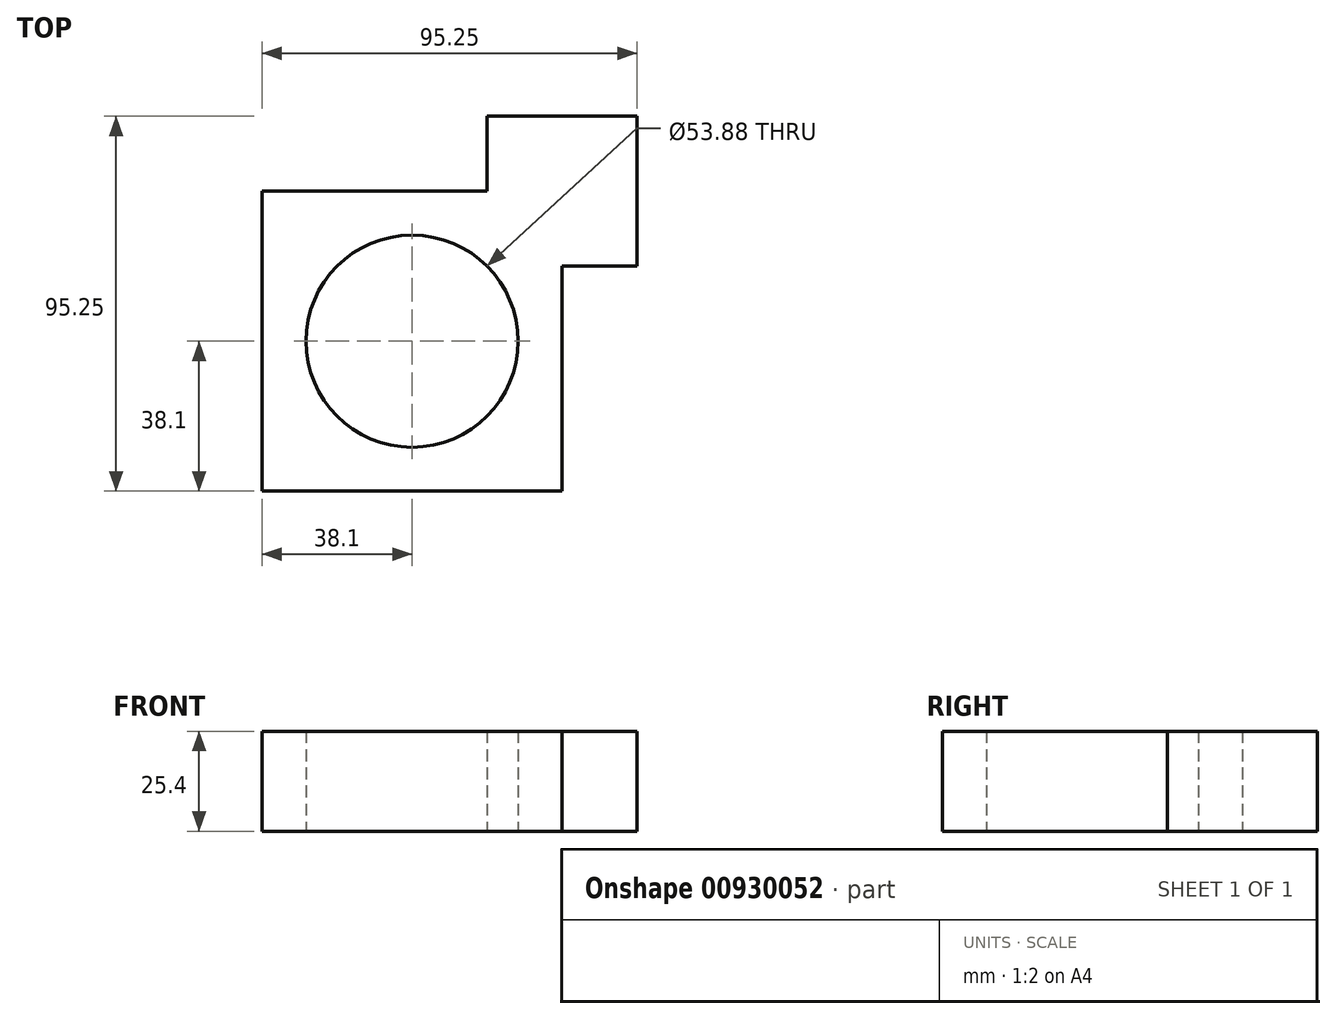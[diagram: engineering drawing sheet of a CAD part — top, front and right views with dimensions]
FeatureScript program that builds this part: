
annotation { "Feature Type Name" : "Feature", "Feature Type Description" : "" }
export const myFeature = defineFeature(function(context is Context, id is Id, definition is map)
    precondition{}
    {
        {
            var Q0;
            Q0=qCreatedBy(makeId("Top.planeOp"),FACE);
            var sketch = newSketch(context, id + "F0", { "sketchPlane" : qUnion([Q0])});
            skLineSegment(sketch, "E0.bottom", {"start": v(0, 0) * mm, "end": v(76.2, 0) * mm});
            skLineSegment(sketch, "E0.top", {"start": v(0, 76.2) * mm, "end": v(57.15, 76.2) * mm});
            skLineSegment(sketch, "E0.left", {"start": v(0, 0) * mm, "end": v(0, 76.2) * mm});
            skLineSegment(sketch, "E0.right", {"start": v(76.2, 0) * mm, "end": v(76.2, 57.15) * mm});
            skCircle(sketch, "E1", {"center": v(38.1, 38.1) * mm, "radius": 26.94 * mm});
            skLineSegment(sketch, "E2", {"start": v(38.1, 76.2) * mm, "end": v(38.1, 0) * mm, "construction": true});
            skLineSegment(sketch, "E3.bottom", {"start": v(57.15, 95.25) * mm, "end": v(95.25, 95.25) * mm});
            skLineSegment(sketch, "E3.top", {"start": v(76.2, 57.15) * mm, "end": v(95.25, 57.15) * mm});
            skLineSegment(sketch, "E3.left", {"start": v(57.15, 95.25) * mm, "end": v(57.15, 76.2) * mm});
            skLineSegment(sketch, "E3.right", {"start": v(95.25, 95.25) * mm, "end": v(95.25, 57.15) * mm});
            skPoint(sketch, "E4.orphan", {"position": v(76.2, 76.2) * mm});
            skLineSegment(sketch, "E5", {"start": v(76.2, 57.15) * mm, "end": v(0, 57.15) * mm, "construction": true});
            skLineSegment(sketch, "E6", {"start": v(76.2, 57.15) * mm, "end": v(76.2, 95.25) * mm, "construction": true});
            skLineSegment(sketch, "E7", {"start": v(57.15, 76.2) * mm, "end": v(57.15, 0) * mm, "construction": true});
            skPoint(sketch, "E8", {"position": v(57.15, 57.15) * mm});
            skLineSegment(sketch, "E9", {"start": v(57.15, 76.2) * mm, "end": v(57.15, 57.15) * mm, "construction": true});
            skLineSegment(sketch, "E10", {"start": v(38.1, 76.2) * mm, "end": v(57.15, 76.2) * mm, "construction": true});
            skLineSegment(sketch, "E11", {"start": v(57.15, 76.2) * mm, "end": v(76.2, 76.2) * mm, "construction": true});
            skSolve(sketch);
        }
        {
            var Q0;
            Q0=makeQuery(id+"F0.imprint","IMPRINT",FACE,{"disambiguationData":[TD([[makeQuery(id+"F0.imprint","IMPRINT",EDGE,{"derivedFrom":sQuery(id+"F0.wireOp",EDGE,"E0.bottom")}),1.0]])]});
            extrude(context, id + "F1", {"entities" : qUnion([Q0]), "depth" : 25.4 * mm, "offsetDistance" : 25.4 * mm});
        }
    });
